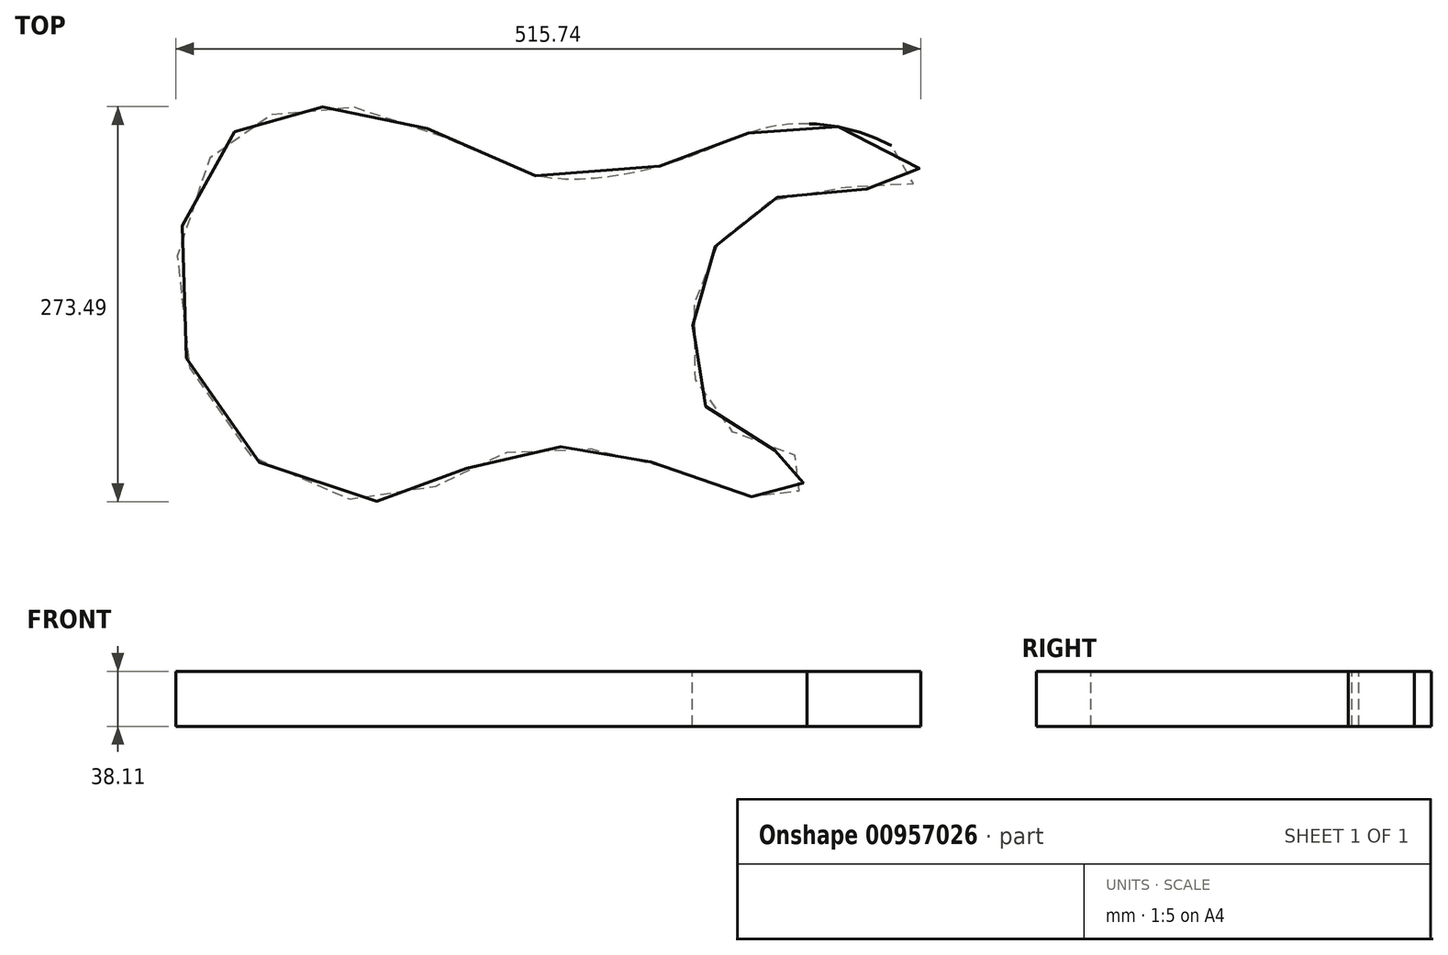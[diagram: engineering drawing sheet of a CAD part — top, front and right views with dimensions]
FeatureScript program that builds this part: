
annotation { "Feature Type Name" : "Feature", "Feature Type Description" : "" }
export const myFeature = defineFeature(function(context is Context, id is Id, definition is map)
    precondition{}
    {
        {
            var Q0;
            Q0=qCreatedBy(makeId("Front.planeOp"),FACE);
            var sketch = newSketch(context, id + "F0", { "sketchPlane" : qUnion([Q0])});
            skLineSegment(sketch, "E0", {"start": v(0, 0) * mm, "end": v(0, 15.88) * mm});
            skLineSegment(sketch, "E1", {"start": v(0, 15.88) * mm, "end": v(634.13, -17.36) * mm});
            skLineSegment(sketch, "E2", {"start": v(634.13, -17.36) * mm, "end": v(633.8, -23.7) * mm});
            skLineSegment(sketch, "E3", {"start": v(633.8, -23.7) * mm, "end": v(0, 9.52) * mm});
            skPoint(sketch, "E3.endSnap0", {"position": v(0, 7.94) * mm});
            skLineSegment(sketch, "E4", {"start": v(181.58, 0) * mm, "end": v(0, 0) * mm});
            skLineSegment(sketch, "E5", {"start": v(633.8, -23.7) * mm, "end": v(638.55, -23.95) * mm});
            skLineSegment(sketch, "E6", {"start": v(638.55, -23.95) * mm, "end": v(836.55, -69.66) * mm});
            skLineSegment(sketch, "E7", {"start": v(152.2, 7.9) * mm, "end": v(151.86, 1.56) * mm});
            skSolve(sketch);
        }
        {
            var Q0;
            Q0=qCreatedBy(makeId("Top.planeOp"),FACE);
            cPlane(context, id + "F1", {"entities" : qUnion([Q0]), "cplaneType" : CPlaneType.OFFSET, "offset" : 9.52 * mm, "oppositeDirection" : true, "width" : 152.4 * mm, "height" : 152.4 * mm});
        }
        {
            var Q0;
            Q0=qCreatedBy(makeId("Top.planeOp"),FACE);
            var sketch = newSketch(context, id + "F2", { "sketchPlane" : qUnion([Q0])});
            skLineSegment(sketch, "E8", {"start": v(181.58, 0) * mm, "end": v(181.58, -181.58) * mm});
            skSolve(sketch);
        }
        {
            var Q0;
            Q0=sQuery(id+"F2.wireOp",EDGE,"E8");
            var Q1;
            Q1=sQuery(id+"F0.wireOp",EDGE,"E3");
            cPlane(context, id + "F3", {"entities" : qUnion([Q0, Q1]), "cplaneType" : CPlaneType.LINE_ANGLE, "offset" : 25.4 * mm, "angle" : 0 * degree, "width" : 152.4 * mm, "height" : 152.4 * mm});
        }
        {
            var Q0;
            Q0=qCreatedBy(id+"F1.planeOp",FACE);
            var sketch = newSketch(context, id + "F4", { "sketchPlane" : qUnion([Q0])});
            skFitSpline(sketch, "E9", {"points": [v(42.6, 91.29) * mm, v(-50.47, 131.7) * mm, v(-128.57, 136.3) * mm, v(-179.48, 108.18) * mm, v(-205.79, 0) * mm, v(-150.58, -105.54) * mm, v(-49.06, -132.12) * mm, v(9.04, -104.3) * mm, v(80, -97.53) * mm, v(140.06, -112.83) * mm, v(211.42, -134.19) * mm, v(224.96, -126.9) * mm, v(229.84, -107.28) * mm, v(209.86, -99.29) * mm, v(164.54, -73.77) * mm, v(151.52, -32.1) * mm, v(158.7, 27.87) * mm, v(181.8, 56.92) * mm, v(229.62, 83.34) * mm, v(289.55, 81.97) * mm, v(309.34, 92.9) * mm, v(268.64, 120.98) * mm, v(201.51, 124.36) * mm, v(150.62, 104.99) * mm, v(42.6, 91.29) * mm]});
            skSolve(sketch);
        }
        {
            var Q0;
            Q0 = qSketchRegion(id + "F4", true);
            extrude(context, id + "F5", {"entities" : qUnion([Q0]), "oppositeDirection" : true, "depth" : 38.1 * mm, "offsetDistance" : 25.4 * mm});
        }
    });
